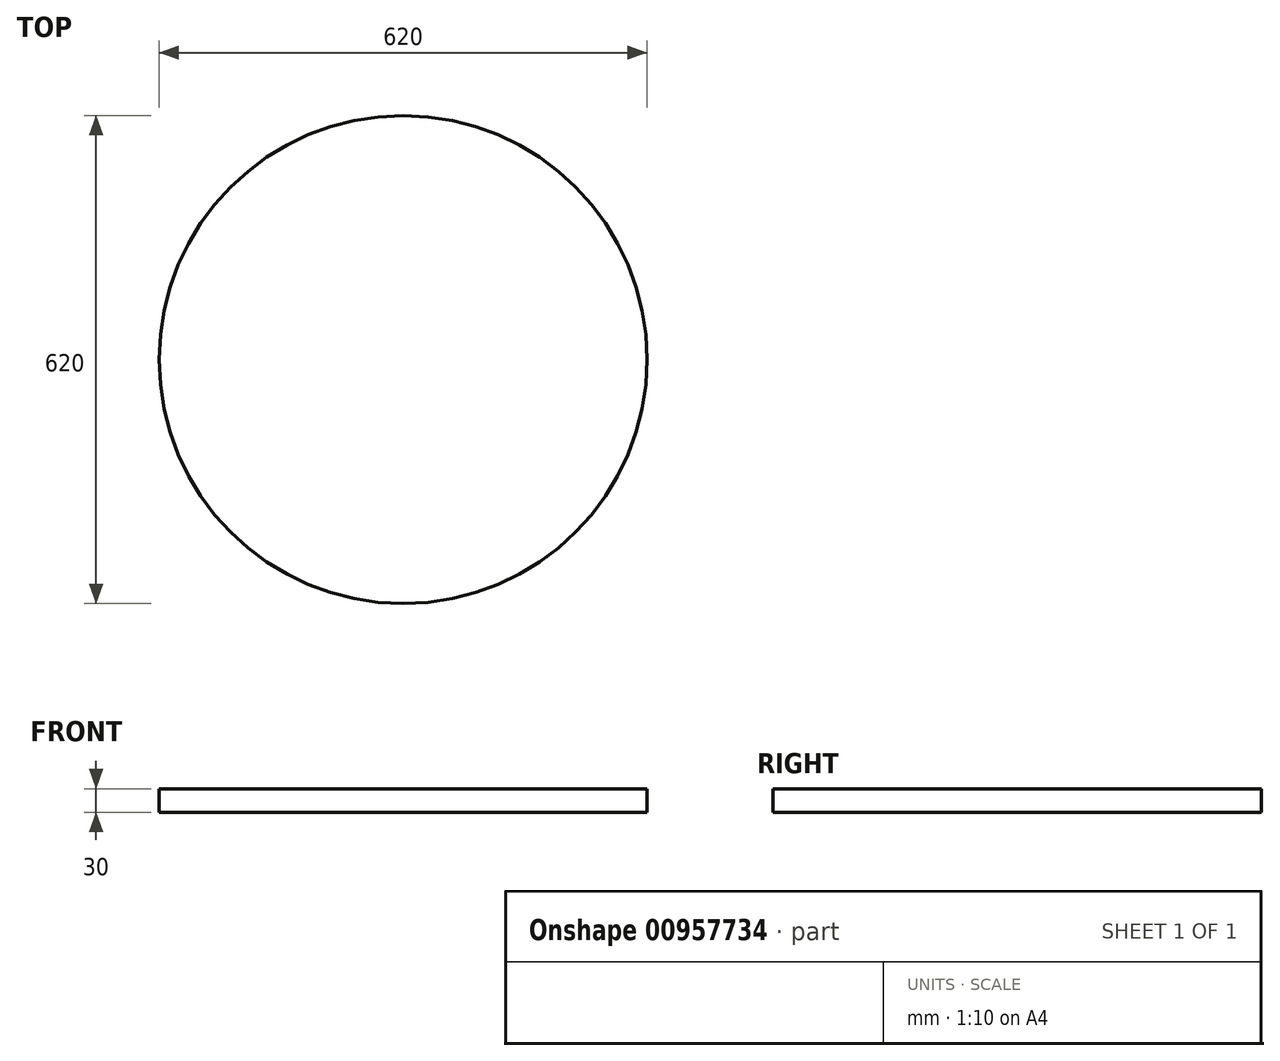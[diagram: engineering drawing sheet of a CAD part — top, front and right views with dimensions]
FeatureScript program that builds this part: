
annotation { "Feature Type Name" : "Feature", "Feature Type Description" : "" }
export const myFeature = defineFeature(function(context is Context, id is Id, definition is map)
    precondition{}
    {
        {
            var Q0;
            Q0=qCreatedBy(makeId("Top.planeOp"),FACE);
            var sketch = newSketch(context, id + "F0", { "sketchPlane" : qUnion([Q0])});
            skCircle(sketch, "E0", {"center": v(0, 0) * mm, "radius": 310 * mm});
            skSolve(sketch);
        }
        {
            var Q0;
            Q0 = qSketchRegion(id + "F0", true);
            extrude(context, id + "F1", {"entities" : qUnion([Q0]), "depth" : 30 * mm, "offsetDistance" : 25 * mm});
        }
    });
